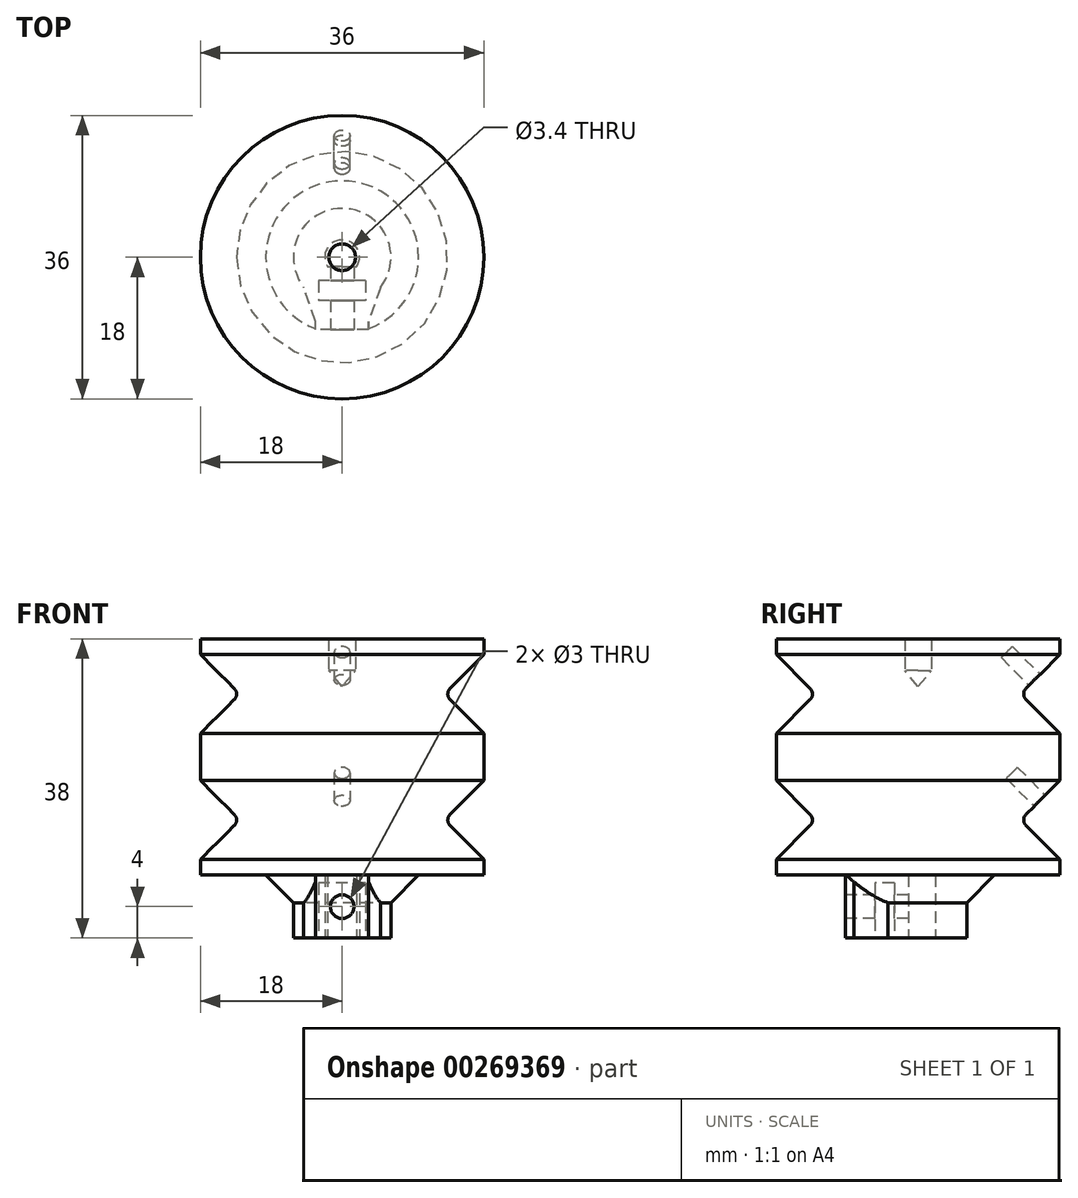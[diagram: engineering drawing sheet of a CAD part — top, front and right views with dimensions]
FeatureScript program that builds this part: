
annotation { "Feature Type Name" : "Feature", "Feature Type Description" : "" }
export const myFeature = defineFeature(function(context is Context, id is Id, definition is map)
    precondition{}
    {
        {
            var Q0;
            Q0=qCreatedBy(makeId("Top.planeOp"),FACE);
            var sketch = newSketch(context, id + "F0", { "sketchPlane" : qUnion([Q0])});
            skArc(sketch, "E0", {"start": v(1.84, -1.2) * mm, "mid": v(0, 2.2) * mm, "end": v(-1.84, -1.2) * mm});
            skLineSegment(sketch, "E1", {"start": v(-1.84, -1.2) * mm, "end": v(1.84, -1.2) * mm});
            skArc(sketch, "E2.0", {"start": v(3.38, -5.2) * mm, "mid": v(0, 6.2) * mm, "end": v(-3.38, -5.2) * mm});
            skLineSegment(sketch, "E2.1", {"start": v(-3.38, -5.2) * mm, "end": v(3.38, -5.2) * mm});
            skSolve(sketch);
        }
        {
            var Q0;
            Q0 = qSketchRegion(id + "F0", true);
            extrude(context, id + "F1", {"entities" : qUnion([Q0]), "depth" : 8 * mm});
        }
        {
            var Q0;
            Q0=makeQuery(id+"F1.opExtrude","SWEPT_FACE",FACE,{"disambiguationData":[OSD([sQuery(id+"F0.wireOp",EDGE,"E2.1")])]});
            cPlane(context, id + "F2", {"entities" : qUnion([Q0]), "cplaneType" : CPlaneType.OFFSET, "offset" : 0 * mm, "width" : 150 * mm, "height" : 150 * mm});
        }
        {
            var Q0;
            Q0=qCreatedBy(id+"F2.planeOp",FACE);
            var sketch = newSketch(context, id + "F3", { "sketchPlane" : qUnion([Q0])});
            skLineSegment(sketch, "E3.bottom", {"start": v(3.38, 0) * mm, "end": v(-3.38, 0) * mm});
            skLineSegment(sketch, "E3.top", {"start": v(3.38, 8) * mm, "end": v(-3.38, 8) * mm});
            skLineSegment(sketch, "E3.left", {"start": v(3.38, 0) * mm, "end": v(3.38, 8) * mm});
            skLineSegment(sketch, "E3.right", {"start": v(-3.38, 0) * mm, "end": v(-3.38, 8) * mm});
            skSolve(sketch);
        }
        {
            var Q0;
            Q0 = qSketchRegion(id + "F3", true);
            extrude(context, id + "F4", {"entities" : qUnion([Q0]), "operationType" : NewBodyOperationType.ADD, "depth" : 4 * mm});
        }
        {
            var Q0;
            Q0=qCreatedBy(makeId("Top.planeOp"),FACE);
            var sketch = newSketch(context, id + "F5", { "sketchPlane" : qUnion([Q0])});
            skLineSegment(sketch, "E4.bottom", {"start": v(3, -3) * mm, "end": v(-3, -3) * mm});
            skLineSegment(sketch, "E4.top", {"start": v(3, -5.5) * mm, "end": v(-3, -5.5) * mm});
            skLineSegment(sketch, "E4.left", {"start": v(3, -3) * mm, "end": v(3, -5.5) * mm});
            skLineSegment(sketch, "E4.right", {"start": v(-3, -3) * mm, "end": v(-3, -5.5) * mm});
            skLineSegment(sketch, "E5", {"start": v(0, 0) * mm, "end": v(0, -3) * mm});
            skSolve(sketch);
        }
        {
            var Q0;
            Q0=qCreatedBy(makeId("Right.planeOp"),FACE);
            var sketch = newSketch(context, id + "F6", { "sketchPlane" : qUnion([Q0])});
            skLineSegment(sketch, "E6", {"start": v(0, 0) * mm, "end": v(0, 8) * mm});
            skLineSegment(sketch, "E7", {"start": v(18, 38) * mm, "end": v(18, 36) * mm});
            skLineSegment(sketch, "E8", {"start": v(18, 26) * mm, "end": v(18, 20) * mm});
            skLineSegment(sketch, "E9", {"start": v(18, 10) * mm, "end": v(18, 8) * mm});
            skLineSegment(sketch, "E10", {"start": v(18, 8) * mm, "end": v(0, 8) * mm});
            skLineSegment(sketch, "E11", {"start": v(18, 36) * mm, "end": v(13.7, 31.7) * mm});
            skLineSegment(sketch, "E12", {"start": v(13.7, 30.3) * mm, "end": v(18, 26) * mm});
            skLineSegment(sketch, "E13", {"start": v(18, 20) * mm, "end": v(13.7, 15.7) * mm});
            skLineSegment(sketch, "E14", {"start": v(13.7, 14.3) * mm, "end": v(18, 10) * mm});
            skPoint(sketch, "E15.visualSharp", {"position": v(13, 31) * mm});
            skArc(sketch, "E15.filletArc", {"start": v(13.7, 31.7) * mm, "mid": v(13.41, 31) * mm, "end": v(13.7, 30.3) * mm});
            skPoint(sketch, "E16.visualSharp", {"position": v(13, 15) * mm});
            skArc(sketch, "E16.filletArc", {"start": v(13.7, 15.7) * mm, "mid": v(13.41, 15) * mm, "end": v(13.7, 14.3) * mm});
            skLineSegment(sketch, "E17", {"start": v(18, 38) * mm, "end": v(1.7, 38) * mm});
            skLineSegment(sketch, "E18", {"start": v(0, 8) * mm, "end": v(0, 31.97) * mm});
            skLineSegment(sketch, "E19", {"start": v(1.7, 38) * mm, "end": v(1.7, 34) * mm});
            skLineSegment(sketch, "E20", {"start": v(1.7, 34) * mm, "end": v(0, 31.97) * mm});
            skPoint(sketch, "E21.orphan", {"position": v(0, 38) * mm});
            skSolve(sketch);
        }
        {
            var Q0;
            Q0 = qSketchRegion(id + "F6", true);
            var Q1;
            Q1=sQuery(id+"F6.wireOp",EDGE,"E18");
            revolve(context, id + "F7", {"operationType" : NewBodyOperationType.ADD, "entities" : qUnion([Q0]), "axis" : qUnion([Q1]), "revolveType" : RevolveType.FULL});
        }
        {
            var Q0;
            Q0 = qSketchRegion(id + "F5", true);
            extrude(context, id + "F8", {"entities" : qUnion([Q0]), "operationType" : NewBodyOperationType.REMOVE, "depth" : 7 * mm});
        }
        {
            var Q0;
            {var subQ0=sQuery(id+"F0.wireOp",EDGE,"E2.1");var subQ1=sQuery(id+"F0.wireOp",EDGE,"E2.0");Q0=makeQuery(id+"F4.boolean.opBoolean","MERGE",EDGE,{"derivedFrom":[makeQuery(id+"F1.opExtrude","SWEPT_EDGE",EDGE,{"disambiguationData":[OSD([subQ1,subQ0]),TDD([makeQuery(id+"F0.imprint","INTERSECT",VERTEX,{"disambiguationData":[OD(1.0)],"derivedFrom":[subQ1,subQ0]})])]}),makeQuery(id+"F4.opExtrude","CAP_EDGE",EDGE,{"disambiguationData":[OSD([sQuery(id+"F3.wireOp",EDGE,"E3.right")])],"isStart":true})]});}
            var Q1;
            {var subQ0=sQuery(id+"F0.wireOp",EDGE,"E2.1");var subQ1=sQuery(id+"F0.wireOp",EDGE,"E2.0");Q1=makeQuery(id+"F4.boolean.opBoolean","MERGE",EDGE,{"derivedFrom":[makeQuery(id+"F1.opExtrude","SWEPT_EDGE",EDGE,{"disambiguationData":[OSD([subQ1,subQ0]),TDD([makeQuery(id+"F0.imprint","INTERSECT",VERTEX,{"disambiguationData":[OD(0.0)],"derivedFrom":[subQ1,subQ0]})])]}),makeQuery(id+"F4.opExtrude","CAP_EDGE",EDGE,{"disambiguationData":[OSD([sQuery(id+"F3.wireOp",EDGE,"E3.left")])],"isStart":true})]});}
            chamfer(context, id + "F9", {"entities" : qUnion([Q0, Q1]), "width" : 7 * mm, "tangentPropagation" : true});
        }
        {
            var Q0;
            Q0=makeQuery(id+"F4.opExtrude","CAP_FACE",FACE,{"disambiguationData":[OSD([sQuery(id+"F3.wireOp",EDGE,"E3.bottom"),sQuery(id+"F3.wireOp",EDGE,"E3.top"),sQuery(id+"F3.wireOp",EDGE,"E3.left"),sQuery(id+"F3.wireOp",EDGE,"E3.right")])],"isStart":false});
            cPlane(context, id + "F10", {"entities" : qUnion([Q0]), "cplaneType" : CPlaneType.OFFSET, "offset" : 0 * mm, "width" : 150 * mm, "height" : 150 * mm});
        }
        {
            var Q0;
            Q0=qCreatedBy(id+"F10.planeOp",FACE);
            var sketch = newSketch(context, id + "F11", { "sketchPlane" : qUnion([Q0])});
            skLineSegment(sketch, "E22", {"start": v(0, 0) * mm, "end": v(0, 4) * mm});
            skCircle(sketch, "E23", {"center": v(0, 4) * mm, "radius": 1.5 * mm});
            skSolve(sketch);
        }
        {
            var Q0;
            Q0 = qSketchRegion(id + "F11", true);
            var Q1;
            Q1=makeQuery(id+"F1.opExtrude","SWEPT_FACE",FACE,{"disambiguationData":[OSD([sQuery(id+"F0.wireOp",EDGE,"E1")])]});
            extrude(context, id + "F12", {"entities" : qUnion([Q0]), "operationType" : NewBodyOperationType.REMOVE, "endBound" : BoundingType.UP_TO_SURFACE, "oppositeDirection" : true, "endBoundEntityFace" : qUnion([Q1]), "depth" : 25 * mm});
        }
        {
            var Q0;
            Q0=makeQuery(id+"F1.opExtrude","CAP_EDGE",EDGE,{"disambiguationData":[OSD([sQuery(id+"F0.wireOp",EDGE,"E2.0")])],"isStart":false});
            chamfer(context, id + "F13", {"entities" : qUnion([Q0]), "width" : 3.5 * mm, "tangentPropagation" : true});
        }
        {
            var Q0;
            Q0=qCreatedBy(makeId("Right.planeOp"),FACE);
            var sketch = newSketch(context, id + "F14", { "sketchPlane" : qUnion([Q0])});
            skLineSegment(sketch, "E24", {"start": v(0, 0) * mm, "end": v(0, 14) * mm});
            skLineSegment(sketch, "E25", {"start": v(0, 14) * mm, "end": v(12, 14) * mm});
            skLineSegment(sketch, "E26", {"start": v(12, 14) * mm, "end": v(15.73, 17.73) * mm});
            skSolve(sketch);
        }
        {
            var Q0;
            Q0=sQuery(id+"F14.wireOp",EDGE,"E26");
            cPlane(context, id + "F15", {"entities" : qUnion([Q0]), "cplaneType" : CPlaneType.LINE_ANGLE, "offset" : 25 * mm, "angle" : 0 * degree, "width" : 150 * mm, "height" : 150 * mm});
        }
        {
            var Q0;
            Q0=qCreatedBy(id+"F15.planeOp",FACE);
            var sketch = newSketch(context, id + "F16", { "sketchPlane" : qUnion([Q0])});
            skCircle(sketch, "E27", {"center": v(0, 23.27) * mm, "radius": 1 * mm});
            skSolve(sketch);
        }
        {
            var Q0;
            Q0=makeQuery(id+"F16.imprint","IMPRINT",FACE,{"disambiguationData":[TD([[makeQuery(id+"F16.imprint","IMPRINT",EDGE,{"derivedFrom":sQuery(id+"F16.wireOp",EDGE,"E27")}),1.0]])]});
            extrude(context, id + "F17", {"entities" : qUnion([Q0]), "operationType" : NewBodyOperationType.REMOVE, "depth" : 5 * mm});
        }
        {
            var Q0;
            Q0=qCreatedBy(makeId("Right.planeOp"),FACE);
            var sketch = newSketch(context, id + "F18", { "sketchPlane" : qUnion([Q0])});
            skLineSegment(sketch, "E28", {"start": v(0, 0) * mm, "end": v(0, 30) * mm});
            skLineSegment(sketch, "E29", {"start": v(0, 30) * mm, "end": v(12, 30) * mm});
            skLineSegment(sketch, "E30", {"start": v(12, 30) * mm, "end": v(15.94, 33.94) * mm});
            skSolve(sketch);
        }
        {
            var Q0;
            Q0=sQuery(id+"F18.wireOp",EDGE,"E30");
            cPlane(context, id + "F19", {"entities" : qUnion([Q0]), "cplaneType" : CPlaneType.LINE_ANGLE, "offset" : 25 * mm, "angle" : 0 * degree, "width" : 150 * mm, "height" : 150 * mm});
        }
        {
            var Q0;
            Q0=qCreatedBy(id+"F19.planeOp",FACE);
            var sketch = newSketch(context, id + "F20", { "sketchPlane" : qUnion([Q0])});
            skCircle(sketch, "E31", {"center": v(0, 33.66) * mm, "radius": 1 * mm});
            skSolve(sketch);
        }
        {
            var Q0;
            Q0 = qSketchRegion(id + "F20", true);
            extrude(context, id + "F21", {"entities" : qUnion([Q0]), "operationType" : NewBodyOperationType.REMOVE, "depth" : 5 * mm});
        }
    });
